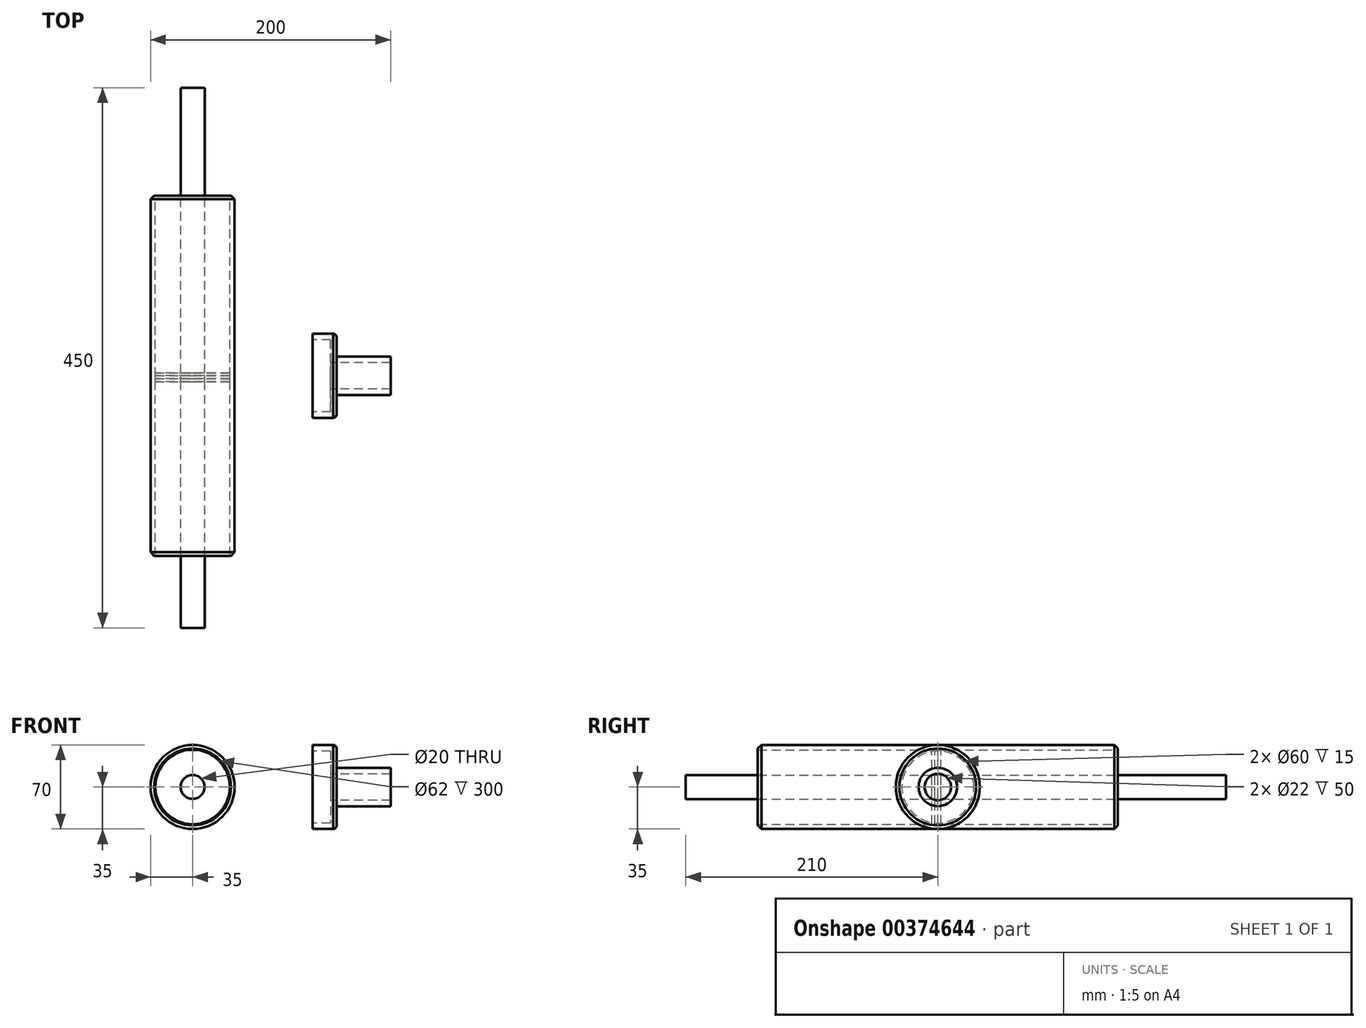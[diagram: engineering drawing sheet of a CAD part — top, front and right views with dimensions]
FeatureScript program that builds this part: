
annotation { "Feature Type Name" : "Feature", "Feature Type Description" : "" }
export const myFeature = defineFeature(function(context is Context, id is Id, definition is map)
    precondition{}
    {
        {
            var Q0;
            Q0=qCreatedBy(makeId("Front.planeOp"),FACE);
            var sketch = newSketch(context, id + "F0", { "sketchPlane" : qUnion([Q0])});
            skCircle(sketch, "E0", {"center": v(0, 0) * mm, "radius": 35 * mm});
            skSolve(sketch);
        }
        {
            var Q0;
            Q0=makeQuery(id+"F0.imprint","IMPRINT",FACE,{"disambiguationData":[TD([[makeQuery(id+"F0.imprint","IMPRINT",EDGE,{"derivedFrom":sQuery(id+"F0.wireOp",EDGE,"E0")}),1.0]])]});
            extrude(context, id + "F1", {"entities" : qUnion([Q0]), "endBound" : BoundingType.SYMMETRIC, "depth" : 300 * mm});
        }
        {
            var Q0;
            Q0=makeQuery(id+"F1.opExtrude","CAP_FACE",FACE,{"disambiguationData":[OSD([sQuery(id+"F0.wireOp",EDGE,"E0")])],"isStart":false});
            var Q1;
            Q1=makeQuery(id+"F1.opExtrude","CAP_FACE",FACE,{"disambiguationData":[OSD([sQuery(id+"F0.wireOp",EDGE,"E0")])],"isStart":true});
            shell(context, id + "F2", {"entities" : qUnion([Q0, Q1]), "thickness" : 4 * mm});
        }
        {
            var Q0;
            Q0=qCreatedBy(makeId("Front.planeOp"),FACE);
            var sketch = newSketch(context, id + "F3", { "sketchPlane" : qUnion([Q0])});
            skCircle(sketch, "E1", {"center": v(0, 0) * mm, "radius": 10 * mm});
            skSolve(sketch);
        }
        {
            var Q0;
            Q0=makeQuery(id+"F3.imprint","IMPRINT",FACE,{"disambiguationData":[TD([[makeQuery(id+"F3.imprint","IMPRINT",EDGE,{"derivedFrom":sQuery(id+"F3.wireOp",EDGE,"E1")}),1.0]])]});
            extrude(context, id + "F4", {"entities" : qUnion([Q0]), "depth" : (420 / 2) * mm, "hasSecondDirection" : true, "secondDirectionOppositeDirection" : true, "secondDirectionDepth" : 240 * mm});
        }
        {
            var Q0;
            Q0=qCreatedBy(makeId("Front.planeOp"),FACE);
            var sketch = newSketch(context, id + "F5", { "sketchPlane" : qUnion([Q0])});
            skCircle(sketch, "E2.0", {"center": v(0, 0) * mm, "radius": 31 * mm});
            skSolve(sketch);
        }
        {
            var Q0;
            Q0 = qSketchRegion(id + "F5", true);
            extrude(context, id + "F6", {"entities" : qUnion([Q0]), "endBound" : BoundingType.SYMMETRIC, "depth" : 5 * mm});
        }
        {
            var Q0;
            Q0=makeQuery(id+"F6.opExtrude","SWEPT_BODY",BODY,{"disambiguationData":[OSD([sQuery(id+"F5.wireOp",EDGE,"E2.0")])]});
            var Q1;
            Q1=makeQuery(id+"F4.opExtrude","SWEPT_BODY",BODY,{"disambiguationData":[OSD([sQuery(id+"F3.wireOp",EDGE,"E1")])]});
            booleanBodies(context, id + "F7", {"operationType" : BooleanOperationType.UNION, "tools" : qUnion([Q0, Q1])});
        }
        {
            var Q0;
            Q0=qCreatedBy(makeId("Front.planeOp"),FACE);
            var sketch = newSketch(context, id + "F8", { "sketchPlane" : qUnion([Q0])});
            skCircle(sketch, "E3.0", {"center": v(0, 0) * mm, "radius": 31 * mm});
            skCircle(sketch, "E4.0", {"center": v(0, 0) * mm, "radius": 10 * mm});
            skSolve(sketch);
        }
        {
            var Q0;
            Q0 = qSketchRegion(id + "F8", true);
            extrude(context, id + "F9", {"entities" : qUnion([Q0]), "depth" : 5 * mm});
        }
        {
            var Q0;
            Q0=qCreatedBy(makeId("Front.planeOp"),FACE);
            var sketch = newSketch(context, id + "F10", { "sketchPlane" : qUnion([Q0])});
            skLineSegment(sketch, "E5", {"start": v(100, 30) * mm, "end": v(115, 30) * mm});
            skLineSegment(sketch, "E6", {"start": v(115, 30) * mm, "end": v(115, 11) * mm});
            skLineSegment(sketch, "E7", {"start": v(115, 11) * mm, "end": v(165, 11) * mm});
            skLineSegment(sketch, "E8.MirrorCS", {"start": v(100, -30) * mm, "end": v(115, -30) * mm});
            skLineSegment(sketch, "E9.MirrorCS", {"start": v(115, -11) * mm, "end": v(165, -11) * mm});
            skLineSegment(sketch, "E10.MirrorCS", {"start": v(115, -30) * mm, "end": v(115, -11) * mm});
            skLineSegment(sketch, "E11.0", {"start": v(120, 16) * mm, "end": v(165, 16) * mm});
            skLineSegment(sketch, "E11.1", {"start": v(120, 35) * mm, "end": v(120, 16) * mm});
            skLineSegment(sketch, "E11.2", {"start": v(100, 35) * mm, "end": v(120, 35) * mm});
            skLineSegment(sketch, "E12", {"start": v(100, 35) * mm, "end": v(100, 30) * mm});
            skLineSegment(sketch, "E13", {"start": v(165, 16) * mm, "end": v(165, 11) * mm});
            skLineSegment(sketch, "E14.MirrorCS", {"start": v(165, -11) * mm, "end": v(165, -16) * mm});
            skLineSegment(sketch, "E15.MirrorCS", {"start": v(100, -30) * mm, "end": v(100, -35) * mm});
            skLineSegment(sketch, "E16.MirrorCS", {"start": v(120, -35) * mm, "end": v(120, -16) * mm});
            skLineSegment(sketch, "E17.MirrorCS", {"start": v(100, -35) * mm, "end": v(120, -35) * mm});
            skLineSegment(sketch, "E18.MirrorCS", {"start": v(120, -16) * mm, "end": v(165, -16) * mm});
            skLineSegment(sketch, "E19", {"start": v(60.64, 0) * mm, "end": v(286.85, 0) * mm, "construction": true});
            skSolve(sketch);
        }
        {
            var Q0;
            Q0 = qSketchRegion(id + "F10", true);
            var Q1;
            Q1=sQuery(id+"F10.wireOp",EDGE,"E19");
            revolve(context, id + "F11", {"entities" : qUnion([Q0]), "axis" : qUnion([Q1]), "revolveType" : RevolveType.FULL});
        }
        {
            var Q0;
            Q0=makeQuery(id+"F1.opExtrude","CAP_EDGE",EDGE,{"disambiguationData":[OSD([sQuery(id+"F0.wireOp",EDGE,"E0")])],"isStart":true});
            var Q1;
            Q1=makeQuery(id+"F11.opRevolve","SWEPT_EDGE",EDGE,{"disambiguationData":[OSD([sQuery(id+"F10.wireOp",EDGE,"E11.1"),sQuery(id+"F10.wireOp",EDGE,"E11.2")])]});
            var Q2;
            Q2=makeQuery(id+"F1.opExtrude","CAP_EDGE",EDGE,{"disambiguationData":[OSD([sQuery(id+"F0.wireOp",EDGE,"E0")])],"isStart":false});
            chamfer(context, id + "F12", {"entities" : qUnion([Q0, Q1, Q2]), "width" : 3 * mm, "tangentPropagation" : true});
        }
        {
            var Q0;
            Q0=makeQuery(id+"F11.opRevolve","SWEPT_EDGE",EDGE,{"disambiguationData":[OSD([sQuery(id+"F10.wireOp",EDGE,"E16.MirrorCS"),sQuery(id+"F10.wireOp",EDGE,"E17.MirrorCS")])]});
            fillet(context, id + "F13", {"entities" : qUnion([Q0]), "radius" : 3 * mm, "tangentPropagation" : true, "allowEdgeOverflow" : false});
        }
    });
